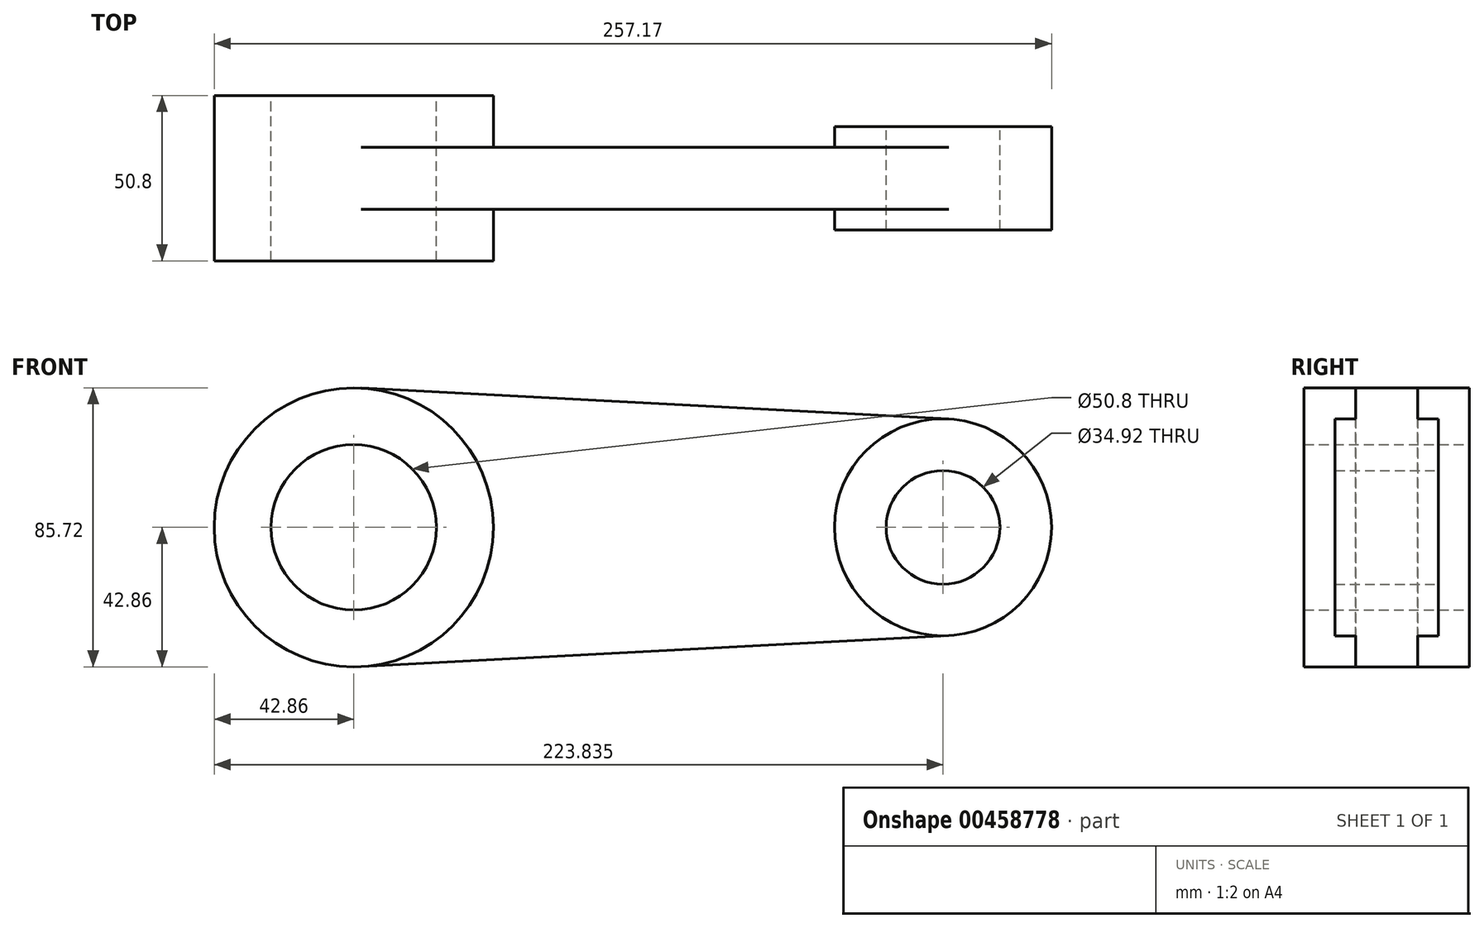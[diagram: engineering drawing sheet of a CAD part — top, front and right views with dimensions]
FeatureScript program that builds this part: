
annotation { "Feature Type Name" : "Feature", "Feature Type Description" : "" }
export const myFeature = defineFeature(function(context is Context, id is Id, definition is map)
    precondition{}
    {
        {
            var Q0;
            Q0=qCreatedBy(makeId("Front.planeOp"),FACE);
            var sketch = newSketch(context, id + "F0", { "sketchPlane" : qUnion([Q0])});
            skCircle(sketch, "E0", {"center": v(0, 0) * mm, "radius": 42.86 * mm});
            skCircle(sketch, "E1", {"center": v(180.98, 0) * mm, "radius": 33.34 * mm});
            skCircle(sketch, "E2", {"center": v(0, 0) * mm, "radius": 25.4 * mm});
            skCircle(sketch, "E3", {"center": v(180.98, 0) * mm, "radius": 17.46 * mm});
            skLineSegment(sketch, "E4", {"start": v(2.26, 42.8) * mm, "end": v(182.73, 33.3) * mm});
            skPoint(sketch, "E5.orphan", {"position": v(180.98, -33.34) * mm});
            skLineSegment(sketch, "E6", {"start": v(182.73, -33.3) * mm, "end": v(2.26, -42.8) * mm});
            skSolve(sketch);
        }
        {
            var Q0;
            Q0=makeQuery(id+"F0.imprint","IMPRINT",FACE,{"disambiguationData":[TD([[makeQuery(id+"F0.imprint","IMPRINT",EDGE,{"derivedFrom":sQuery(id+"F0.wireOp",EDGE,"E2")}),-1.0]])]});
            extrude(context, id + "F1", {"entities" : qUnion([Q0]), "depth" : 50.8 * mm, "symmetric" : true});
        }
        {
            var Q0;
            {var subQ0=sQuery(id+"F0.wireOp",EDGE,"PnOSwK1Q-zJZm-aGDa-PyPT-2nZ57jDV0lPq");var subQ1=sQuery(id+"F0.wireOp",EDGE,"E0");var subQ2=makeQuery(id+"F0.imprint","INTERSECT",VERTEX,{"derivedFrom":[subQ1,subQ0]});Q0=makeQuery(id+"F0.imprint","IMPRINT",FACE,{"disambiguationData":[TD([[makeQuery(id+"F0.imprint","IMPRINT",EDGE,{"disambiguationData":[TD([[subQ2,-1.0]])],"derivedFrom":subQ1}),-1.0]])]});}
            extrude(context, id + "F2", {"entities" : qUnion([Q0]), "operationType" : NewBodyOperationType.ADD, "depth" : 19.05 * mm, "symmetric" : true});
        }
        {
            var Q0;
            Q0=makeQuery(id+"F0.imprint","IMPRINT",FACE,{"disambiguationData":[TD([[makeQuery(id+"F0.imprint","IMPRINT",EDGE,{"derivedFrom":sQuery(id+"F0.wireOp",EDGE,"E3")}),-1.0]])]});
            extrude(context, id + "F3", {"entities" : qUnion([Q0]), "operationType" : NewBodyOperationType.ADD, "depth" : 31.75 * mm, "symmetric" : true});
        }
    });
